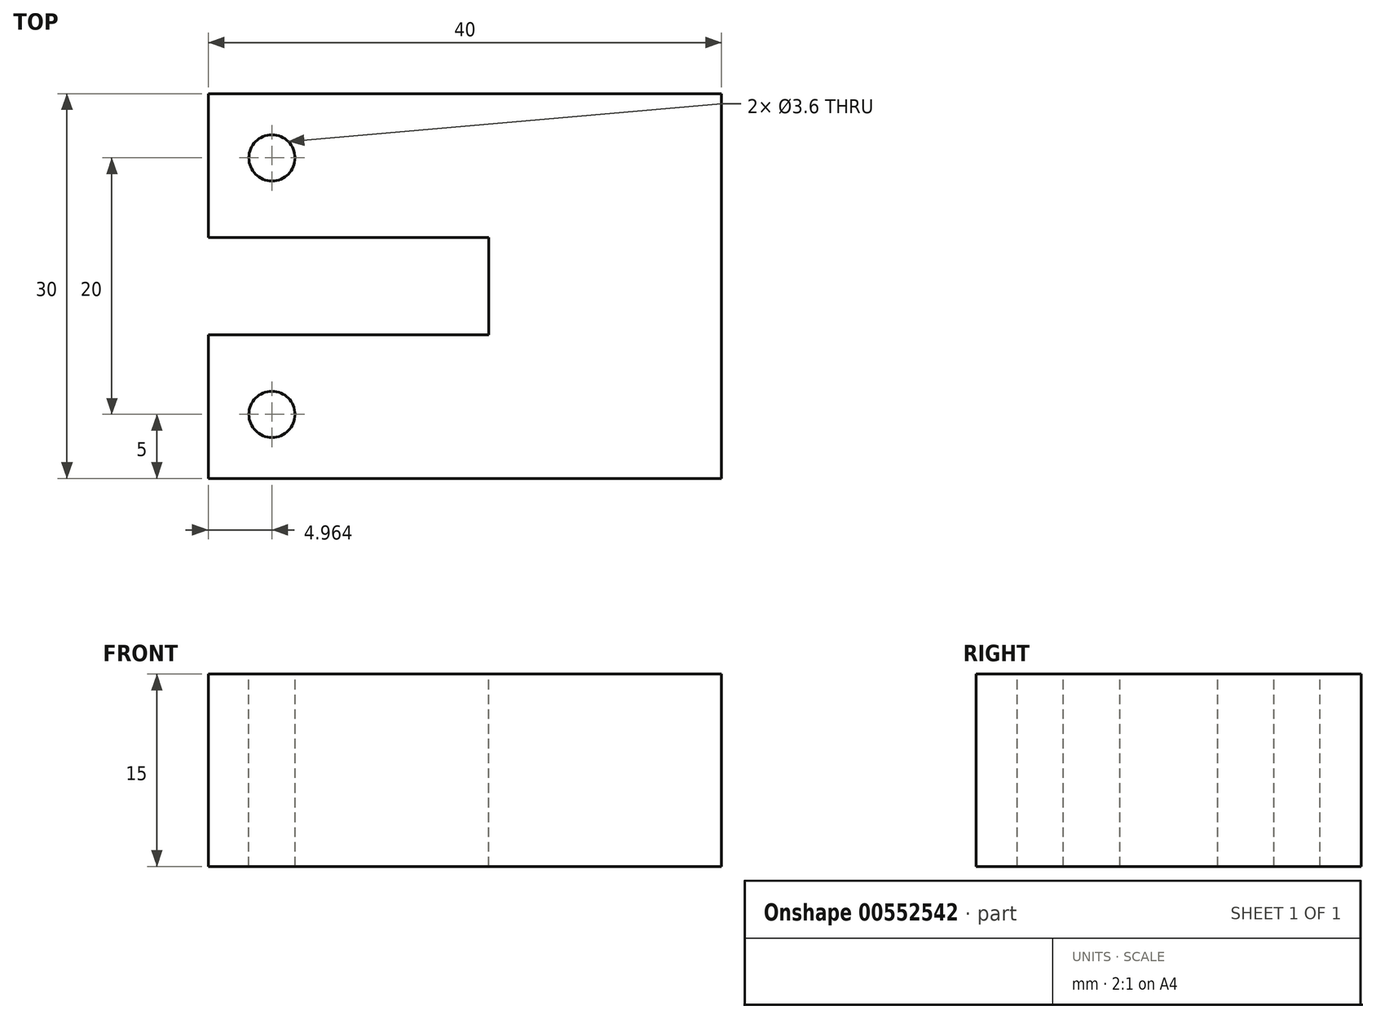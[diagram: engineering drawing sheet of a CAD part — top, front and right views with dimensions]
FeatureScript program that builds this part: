
annotation { "Feature Type Name" : "Feature", "Feature Type Description" : "" }
export const myFeature = defineFeature(function(context is Context, id is Id, definition is map)
    precondition{}
    {
        {
            var Q0;
            Q0=qCreatedBy(makeId("Top.planeOp"),FACE);
            var sketch = newSketch(context, id + "F0", { "sketchPlane" : qUnion([Q0])});
            skLineSegment(sketch, "E0.bottom", {"start": v(20, 15) * mm, "end": v(-20, 15) * mm});
            skLineSegment(sketch, "E0.top", {"start": v(20, -15) * mm, "end": v(-20, -15) * mm});
            skLineSegment(sketch, "E0.left", {"start": v(20, 15) * mm, "end": v(20, -15) * mm});
            skLineSegment(sketch, "E0.right", {"start": v(-20, 15) * mm, "end": v(-20, -15) * mm});
            skPoint(sketch, "E0.middle", {"position": v(0, 0) * mm});
            skSolve(sketch);
        }
        {
            var Q0;
            Q0 = qSketchRegion(id + "F0", true);
            extrude(context, id + "F1", {"entities" : qUnion([Q0]), "endBound" : BoundingType.SYMMETRIC, "depth" : 15 * mm, "offsetDistance" : 25 * mm});
        }
        {
            var Q0;
            Q0=makeQuery(id+"F1.opExtrude","CAP_FACE",FACE,{"disambiguationData":[OSD([sQuery(id+"F0.wireOp",EDGE,"E0.bottom"),sQuery(id+"F0.wireOp",EDGE,"E0.top"),sQuery(id+"F0.wireOp",EDGE,"E0.left"),sQuery(id+"F0.wireOp",EDGE,"E0.right")])],"isStart":false});
            var sketch = newSketch(context, id + "F2", { "sketchPlane" : qUnion([Q0])});
            skLineSegment(sketch, "E1.bottom", {"start": v(-20, 3.8) * mm, "end": v(1.86, 3.8) * mm});
            skLineSegment(sketch, "E1.top", {"start": v(-20, -3.8) * mm, "end": v(1.86, -3.8) * mm});
            skLineSegment(sketch, "E1.left", {"start": v(-20, 3.8) * mm, "end": v(-20, -3.8) * mm});
            skLineSegment(sketch, "E1.right", {"start": v(1.86, 3.8) * mm, "end": v(1.86, -3.8) * mm});
            skPoint(sketch, "E1.middle", {"position": v(-9.07, 0) * mm});
            skSolve(sketch);
        }
        {
            var Q0;
            Q0 = qSketchRegion(id + "F2", true);
            extrude(context, id + "F3", {"entities" : qUnion([Q0]), "operationType" : NewBodyOperationType.REMOVE, "oppositeDirection" : true, "depth" : 25 * mm, "offsetDistance" : 25 * mm});
        }
        {
            var Q0;
            Q0=makeQuery(id+"F1.opExtrude","CAP_FACE",FACE,{"disambiguationData":[OSD([sQuery(id+"F0.wireOp",EDGE,"E0.bottom"),sQuery(id+"F0.wireOp",EDGE,"E0.top"),sQuery(id+"F0.wireOp",EDGE,"E0.left"),sQuery(id+"F0.wireOp",EDGE,"E0.right")])],"isStart":false});
            var sketch = newSketch(context, id + "F4", { "sketchPlane" : qUnion([Q0])});
            skCircle(sketch, "E2", {"center": v(-15.04, -10) * mm, "radius": 1.8 * mm});
            skCircle(sketch, "E3", {"center": v(-15.04, 10) * mm, "radius": 1.8 * mm});
            skSolve(sketch);
        }
        {
            var Q0;
            Q0 = qSketchRegion(id + "F4", true);
            extrude(context, id + "F5", {"entities" : qUnion([Q0]), "operationType" : NewBodyOperationType.REMOVE, "oppositeDirection" : true, "depth" : 20 * mm, "offsetDistance" : 25 * mm});
        }
    });
